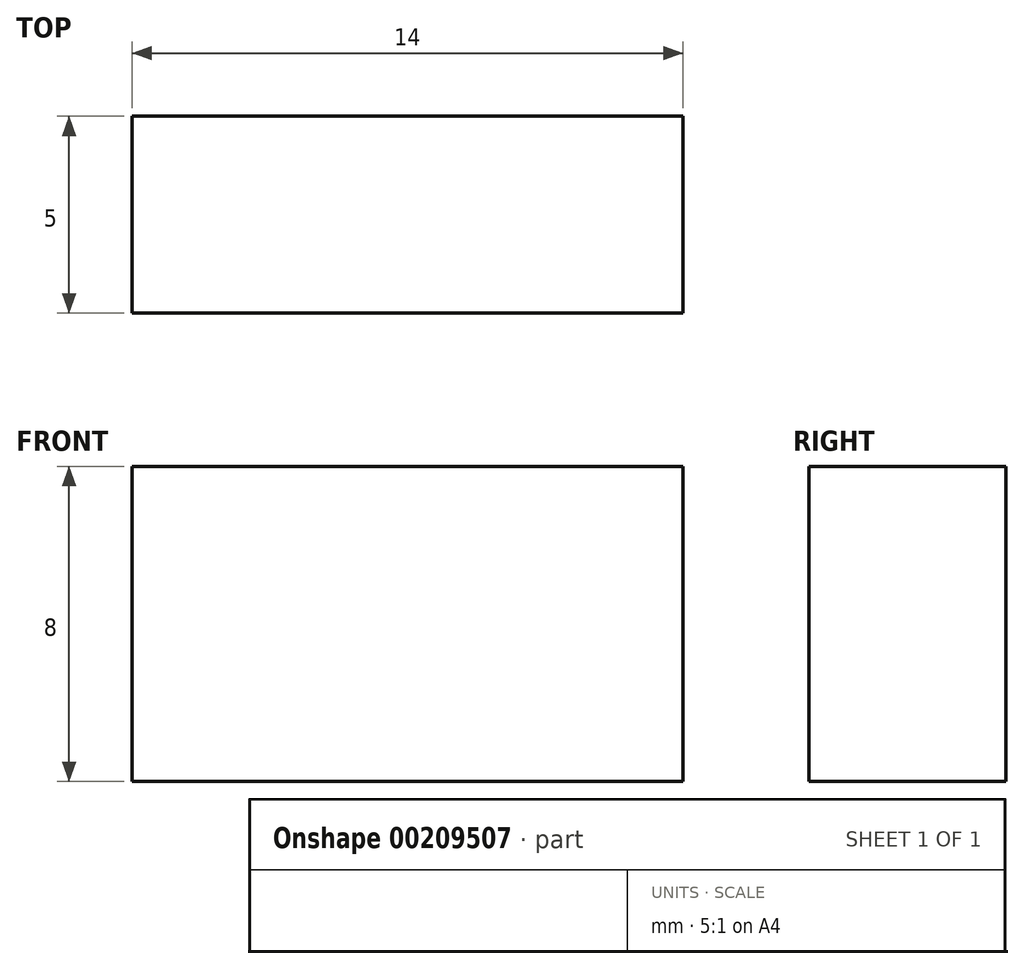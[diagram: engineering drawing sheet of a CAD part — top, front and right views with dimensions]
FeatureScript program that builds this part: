
annotation { "Feature Type Name" : "Feature", "Feature Type Description" : "" }
export const myFeature = defineFeature(function(context is Context, id is Id, definition is map)
    precondition{}
    {
        {
            var Q0;
            Q0=qCreatedBy(makeId("Top.planeOp"),FACE);
            var sketch = newSketch(context, id + "F0", { "sketchPlane" : qUnion([Q0])});
            skLineSegment(sketch, "E0.bottom", {"start": v(-7, 2.5) * mm, "end": v(7, 2.5) * mm});
            skLineSegment(sketch, "E0.top", {"start": v(-7, -2.5) * mm, "end": v(7, -2.5) * mm});
            skLineSegment(sketch, "E0.left", {"start": v(-7, 2.5) * mm, "end": v(-7, -2.5) * mm});
            skLineSegment(sketch, "E0.right", {"start": v(7, 2.5) * mm, "end": v(7, -2.5) * mm});
            skPoint(sketch, "E0.middle", {"position": v(0, 0) * mm});
            skSolve(sketch);
        }
        {
            var Q0;
            Q0 = qSketchRegion(id + "F0", true);
            extrude(context, id + "F1", {"entities" : qUnion([Q0]), "depth" : 8 * mm});
        }
    });
